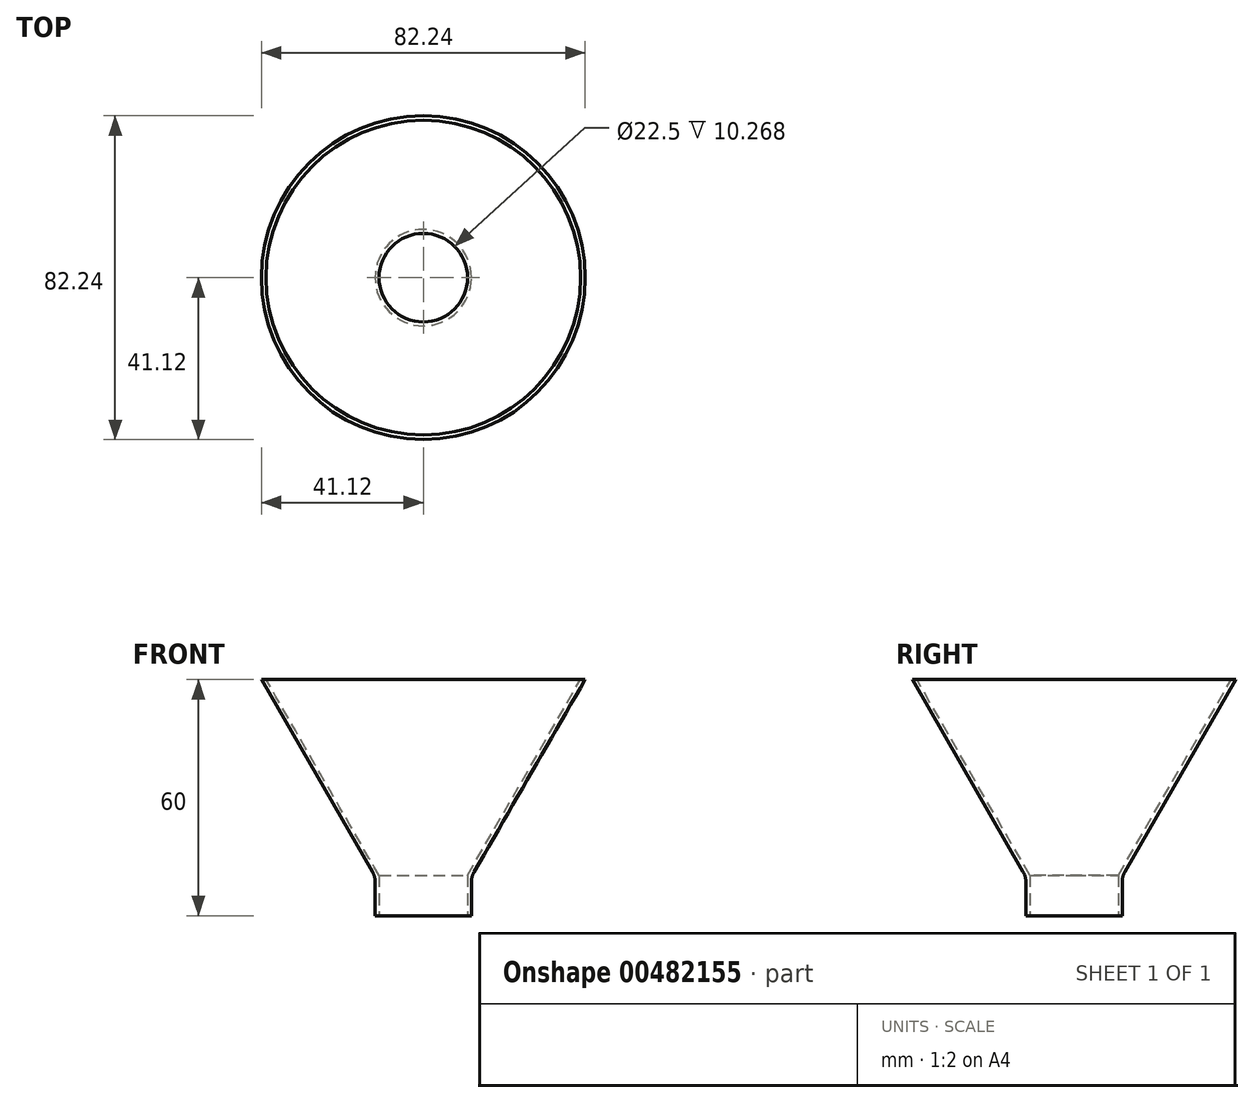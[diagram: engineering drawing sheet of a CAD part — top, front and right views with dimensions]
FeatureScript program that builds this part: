
annotation { "Feature Type Name" : "Feature", "Feature Type Description" : "" }
export const myFeature = defineFeature(function(context is Context, id is Id, definition is map)
    precondition{}
    {
        {
            var Q0;
            Q0=qCreatedBy(makeId("Right.planeOp"),FACE);
            var sketch = newSketch(context, id + "F0", { "sketchPlane" : qUnion([Q0])});
            skLineSegment(sketch, "E0", {"start": v(12.25, 0) * mm, "end": v(12.25, 10) * mm});
            skLineSegment(sketch, "E1", {"start": v(12.25, 10) * mm, "end": v(41.12, 60) * mm});
            skLineSegment(sketch, "E2", {"start": v(12.25, 0) * mm, "end": v(11.25, 0) * mm});
            skLineSegment(sketch, "E3", {"start": v(11.25, 0) * mm, "end": v(11.25, 10.27) * mm});
            skLineSegment(sketch, "E4.0", {"start": v(11.25, 10.27) * mm, "end": v(39.96, 60) * mm});
            skLineSegment(sketch, "E5", {"start": v(39.96, 60) * mm, "end": v(41.12, 60) * mm});
            skSolve(sketch);
        }
        {
            var Q0;
            Q0=qCreatedBy(makeId("Right.planeOp"),FACE);
            var sketch = newSketch(context, id + "F1", { "sketchPlane" : qUnion([Q0])});
            skLineSegment(sketch, "E6", {"start": v(0, 0) * mm, "end": v(0, 47.14) * mm, "construction": true});
            skSolve(sketch);
        }
        {
            var Q0;
            Q0 = qSketchRegion(id + "F0", true);
            var Q1;
            Q1=sQuery(id+"F1.wireOp",EDGE,"E6");
            revolve(context, id + "F2", {"entities" : qUnion([Q0]), "axis" : qUnion([Q1]), "revolveType" : RevolveType.FULL});
        }
        {
            var Q0;
            Q0=makeQuery(id+"F2.opRevolve","SWEPT_EDGE",EDGE,{"disambiguationData":[OSD([sQuery(id+"F0.wireOp",EDGE,"E0"),sQuery(id+"F0.wireOp",EDGE,"E1")])]});
            fillet(context, id + "F3", {"entities" : qUnion([Q0]), "radius" : 5 * mm, "tangentPropagation" : true, "allowEdgeOverflow" : false});
        }
    });
